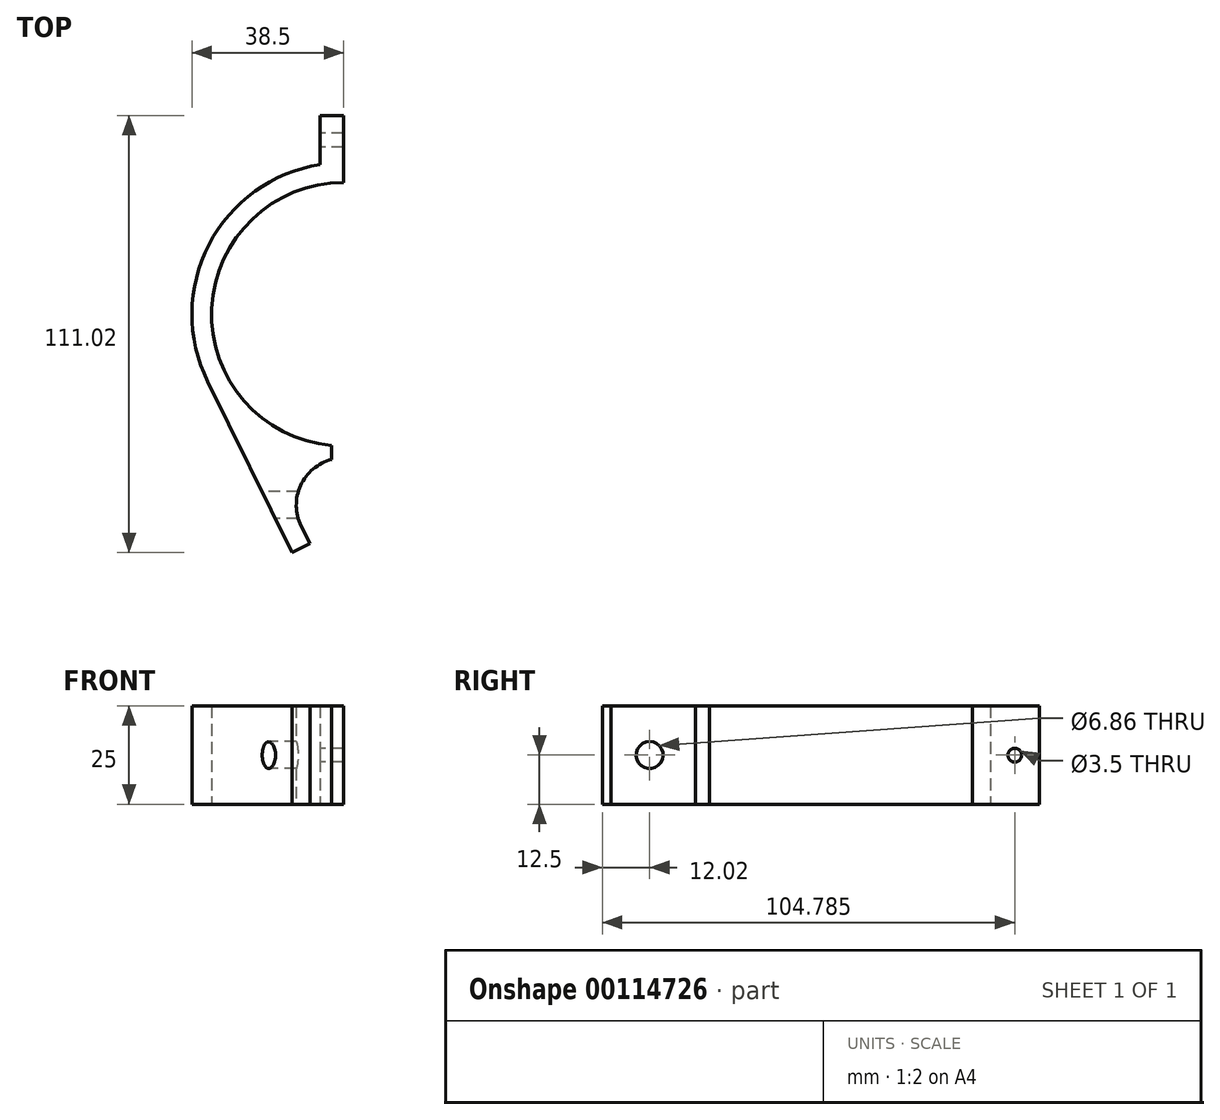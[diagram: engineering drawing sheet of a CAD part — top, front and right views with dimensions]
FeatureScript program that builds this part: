
annotation { "Feature Type Name" : "Feature", "Feature Type Description" : "" }
export const myFeature = defineFeature(function(context is Context, id is Id, definition is map)
    precondition{}
    {
        {
            var Q0;
            Q0=qCreatedBy(makeId("Top.planeOp"),FACE);
            var sketch = newSketch(context, id + "F0", { "sketchPlane" : qUnion([Q0])});
            skCircle(sketch, "E0", {"center": v(0, 0) * mm, "radius": 12 * mm});
            skCircle(sketch, "E1", {"center": v(0, 48.5) * mm, "radius": 33.5 * mm});
            skLineSegment(sketch, "E2.0", {"start": v(-34.51, 31.43) * mm, "end": v(-15.24, -7.54) * mm});
            skLineSegment(sketch, "E3.0", {"start": v(15.24, -7.54) * mm, "end": v(34.51, 31.43) * mm});
            skArc(sketch, "E4.0", {"start": v(-15.24, -7.54) * mm, "mid": v(0, -17) * mm, "end": v(15.24, -7.54) * mm});
            skArc(sketch, "E5.trimOffspring", {"start": v(34.51, 31.43) * mm, "mid": v(0, 87) * mm, "end": v(-34.51, 31.43) * mm});
            skSolve(sketch);
        }
        {
            var Q0;
            Q0 = qSketchRegion(id + "F0", true);
            extrude(context, id + "F1", {"entities" : qUnion([Q0]), "depth" : 50 * mm});
        }
        {
            var Q0;
            Q0=qCreatedBy(makeId("Front.planeOp"),FACE);
            cPlane(context, id + "F2", {"entities" : qUnion([Q0]), "cplaneType" : CPlaneType.OFFSET, "offset" : 87 * mm, "oppositeDirection" : true, "width" : 150 * mm, "height" : 150 * mm});
        }
        {
            var Q0;
            Q0=qCreatedBy(id+"F2.planeOp",FACE);
            var sketch = newSketch(context, id + "F3", { "sketchPlane" : qUnion([Q0])});
            skLineSegment(sketch, "E6.0", {"start": v(-38.5, 50) * mm, "end": v(38.5, 50) * mm});
            skEllipse(sketch, "E7", {"center": v(0, 50) * mm, "majorRadius": 23 * mm, "minorRadius": 17.5 * mm, "majorAxis": v(0, -1)});
            skSolve(sketch);
        }
        {
            var Q0;
            Q0 = qSketchRegion(id + "F3", true);
            extrude(context, id + "F4", {"entities" : qUnion([Q0]), "operationType" : NewBodyOperationType.REMOVE, "depth" : 25 * mm});
        }
        {
            var Q0;
            Q0=qCreatedBy(id+"F2.planeOp",FACE);
            var sketch = newSketch(context, id + "F5", { "sketchPlane" : qUnion([Q0])});
            skLineSegment(sketch, "E8.bottom", {"start": v(6, 0) * mm, "end": v(-6, 0) * mm});
            skLineSegment(sketch, "E8.top", {"start": v(6, 25) * mm, "end": v(-6, 25) * mm});
            skLineSegment(sketch, "E8.left", {"start": v(6, 0) * mm, "end": v(6, 25) * mm});
            skLineSegment(sketch, "E8.right", {"start": v(-6, 0) * mm, "end": v(-6, 25) * mm});
            skSolve(sketch);
        }
        {
            var Q0;
            Q0 = qSketchRegion(id + "F5", true);
            extrude(context, id + "F6", {"entities" : qUnion([Q0]), "operationType" : NewBodyOperationType.ADD, "depth" : 1 * mm});
        }
        {
            var Q0;
            Q0 = qSketchRegion(id + "F5", true);
            extrude(context, id + "F7", {"entities" : qUnion([Q0]), "operationType" : NewBodyOperationType.ADD, "oppositeDirection" : true, "depth" : 12 * mm});
        }
        {
            var Q0;
            Q0=qCreatedBy(makeId("Right.planeOp"),FACE);
            var sketch = newSketch(context, id + "F8", { "sketchPlane" : qUnion([Q0])});
            skLineSegment(sketch, "E9.0", {"start": v(31.43, 50) * mm, "end": v(-7.54, 50) * mm});
            skLineSegment(sketch, "E10.0", {"start": v(31.43, 0) * mm, "end": v(-7.54, 0) * mm});
            skPoint(sketch, "E11", {"position": v(0, 50) * mm});
            skLineSegment(sketch, "E12", {"start": v(0, 50) * mm, "end": v(0, 0) * mm, "construction": true});
            skLineSegment(sketch, "E13.0", {"start": v(86.53, 25) * mm, "end": v(99, 25) * mm, "construction": true});
            skPoint(sketch, "E14.center.orphan", {"position": v(0, 25) * mm});
            skLineSegment(sketch, "E15", {"start": v(86.53, 25) * mm, "end": v(0, 25) * mm, "construction": true});
            skLineSegment(sketch, "E16", {"start": v(0, 25) * mm, "end": v(0, 0) * mm, "construction": true});
            skCircle(sketch, "E17", {"center": v(0, 12.5) * mm, "radius": 3.43 * mm});
            skSolve(sketch);
        }
        {
            var Q0;
            Q0 = qSketchRegion(id + "F8", true);
            extrude(context, id + "F9", {"entities" : qUnion([Q0]), "operationType" : NewBodyOperationType.REMOVE, "endBound" : BoundingType.SYMMETRIC, "depth" : 60 * mm});
        }
        {
            var Q0;
            {var subQ0=sQuery(id+"F5.wireOp",EDGE,"E8.right");Q0=makeQuery(id+"F7.boolean.opBoolean","MERGE",FACE,{"derivedFrom":[makeQuery(id+"F6.opExtrude","SWEPT_FACE",FACE,{"disambiguationData":[OSD([subQ0])]}),makeQuery(id+"F7.opExtrude","SWEPT_FACE",FACE,{"disambiguationData":[OSD([subQ0])]})]});}
            var sketch = newSketch(context, id + "F10", { "sketchPlane" : qUnion([Q0])});
            skLineSegment(sketch, "E18", {"start": v(-92.76, 25) * mm, "end": v(-92.76, 0) * mm, "construction": true});
            skLineSegment(sketch, "E19", {"start": v(-99, 12.5) * mm, "end": v(-92.76, 12.5) * mm, "construction": true});
            skCircle(sketch, "E20", {"center": v(-92.76, 12.5) * mm, "radius": 1.75 * mm});
            skPoint(sketch, "E21.0.start.orphan", {"position": v(-86.53, 25) * mm});
            skPoint(sketch, "E22.orphan", {"position": v(-99, 25) * mm});
            skPoint(sketch, "E23.orphan", {"position": v(-99, 0) * mm});
            skPoint(sketch, "E24.0.start.orphan", {"position": v(-86.53, 0) * mm});
            skSolve(sketch);
        }
        {
            var Q0;
            Q0 = qSketchRegion(id + "F10", true);
            extrude(context, id + "F11", {"entities" : qUnion([Q0]), "operationType" : NewBodyOperationType.REMOVE, "oppositeDirection" : true, "depth" : 25 * mm});
        }
        {
            var Q0;
            Q0=makeQuery(id+"F1.opExtrude","CAP_FACE",FACE,{"disambiguationData":[OSD([sQuery(id+"F0.wireOp",EDGE,"E0"),sQuery(id+"F0.wireOp",EDGE,"E1"),sQuery(id+"F0.wireOp",EDGE,"E2.0"),sQuery(id+"F0.wireOp",EDGE,"E3.0"),sQuery(id+"F0.wireOp",EDGE,"E4.0"),sQuery(id+"F0.wireOp",EDGE,"E5.trimOffspring")])],"isStart":false});
            var sketch = newSketch(context, id + "F12", { "sketchPlane" : qUnion([Q0])});
            skLineSegment(sketch, "E25.bottom", {"start": v(-3, 17.8) * mm, "end": v(3, 17.8) * mm});
            skLineSegment(sketch, "E25.top", {"start": v(-3, 9.03) * mm, "end": v(3, 9.03) * mm});
            skLineSegment(sketch, "E25.left", {"start": v(-3, 17.8) * mm, "end": v(-3, 9.03) * mm});
            skLineSegment(sketch, "E25.right", {"start": v(3, 17.8) * mm, "end": v(3, 9.03) * mm});
            skSolve(sketch);
        }
        {
            var Q0;
            Q0 = qSketchRegion(id + "F12", true);
            extrude(context, id + "F13", {"entities" : qUnion([Q0]), "operationType" : NewBodyOperationType.REMOVE, "oppositeDirection" : true, "depth" : 55 * mm});
        }
        {
            var Q0;
            Q0=makeQuery(id+"F1.opExtrude","CAP_FACE",FACE,{"disambiguationData":[OSD([sQuery(id+"F0.wireOp",EDGE,"E0"),sQuery(id+"F0.wireOp",EDGE,"E1"),sQuery(id+"F0.wireOp",EDGE,"E2.0"),sQuery(id+"F0.wireOp",EDGE,"E3.0"),sQuery(id+"F0.wireOp",EDGE,"E4.0"),sQuery(id+"F0.wireOp",EDGE,"E5.trimOffspring")])],"isStart":false});
            var sketch = newSketch(context, id + "F14", { "sketchPlane" : qUnion([Q0])});
            skArc(sketch, "E26.0", {"start": v(-10.76, -5.32) * mm, "mid": v(0, -12) * mm, "end": v(10.76, -5.32) * mm});
            skArc(sketch, "E27.0", {"start": v(-15.24, -7.54) * mm, "mid": v(0, -17) * mm, "end": v(15.24, -7.54) * mm});
            skLineSegment(sketch, "E28", {"start": v(-15.24, -7.54) * mm, "end": v(-10.76, -5.32) * mm});
            skLineSegment(sketch, "E29", {"start": v(15.24, -7.54) * mm, "end": v(10.76, -5.32) * mm});
            skPoint(sketch, "E30.orphan", {"position": v(3, 11.62) * mm});
            skPoint(sketch, "E31.orphan", {"position": v(-3, 11.62) * mm});
            skSolve(sketch);
        }
        {
            var Q0;
            Q0 = qSketchRegion(id + "F14", true);
            extrude(context, id + "F15", {"entities" : qUnion([Q0]), "operationType" : NewBodyOperationType.REMOVE, "oppositeDirection" : true, "depth" : 52 * mm});
        }
        {
            var Q0;
            Q0=qCreatedBy(makeId("Top.planeOp"),FACE);
            var sketch = newSketch(context, id + "F16", { "sketchPlane" : qUnion([Q0])});
            skLineSegment(sketch, "E32.0", {"start": v(-15.24, -7.54) * mm, "end": v(-10.76, -5.32) * mm});
            skLineSegment(sketch, "E33", {"start": v(-15.24, -7.54) * mm, "end": v(-13.02, -12.02) * mm});
            skLineSegment(sketch, "E34", {"start": v(-10.76, -5.32) * mm, "end": v(-8.54, -9.8) * mm});
            skLineSegment(sketch, "E35", {"start": v(-13.02, -12.02) * mm, "end": v(-8.54, -9.8) * mm});
            skPoint(sketch, "E36.0.end.orphan", {"position": v(10.76, -5.32) * mm});
            skPoint(sketch, "E37.0.end.orphan", {"position": v(34.51, 31.43) * mm});
            skPoint(sketch, "E37.0.start.orphan", {"position": v(15.24, -7.54) * mm});
            skPoint(sketch, "E38.0.start.orphan", {"position": v(-34.51, 31.43) * mm});
            skLineSegment(sketch, "E39.MirrorCS", {"start": v(15.24, -7.54) * mm, "end": v(10.76, -5.32) * mm});
            skLineSegment(sketch, "E40.MirrorCS", {"start": v(10.76, -5.32) * mm, "end": v(8.54, -9.8) * mm});
            skLineSegment(sketch, "E41.MirrorCS", {"start": v(13.02, -12.02) * mm, "end": v(8.54, -9.8) * mm});
            skLineSegment(sketch, "E42.MirrorCS", {"start": v(15.24, -7.54) * mm, "end": v(13.02, -12.02) * mm});
            skSolve(sketch);
        }
        {
            var Q0;
            Q0 = qSketchRegion(id + "F16", true);
            extrude(context, id + "F17", {"entities" : qUnion([Q0]), "operationType" : NewBodyOperationType.ADD, "depth" : 50 * mm});
        }
        {
            var Q0;
            Q0=qCreatedBy(makeId("Top.planeOp"),FACE);
            var sketch = newSketch(context, id + "F18", { "sketchPlane" : qUnion([Q0])});
            skLineSegment(sketch, "E43.bottom", {"start": v(0, -47.13) * mm, "end": v(81.3, -47.13) * mm});
            skLineSegment(sketch, "E43.top", {"start": v(0, 114.66) * mm, "end": v(81.3, 114.66) * mm});
            skLineSegment(sketch, "E43.left", {"start": v(0, -47.13) * mm, "end": v(0, 114.66) * mm});
            skLineSegment(sketch, "E43.right", {"start": v(81.3, -47.13) * mm, "end": v(81.3, 114.66) * mm});
            skSolve(sketch);
        }
        {
            var Q0;
            Q0 = qSketchRegion(id + "F18", true);
            extrude(context, id + "F19", {"entities" : qUnion([Q0]), "operationType" : NewBodyOperationType.REMOVE, "depth" : 50 * mm});
        }
        {
            var Q0;
            Q0=qCreatedBy(makeId("Front.planeOp"),FACE);
            var sketch = newSketch(context, id + "F20", { "sketchPlane" : qUnion([Q0])});
            skPoint(sketch, "E44.0", {"position": v(0, 25) * mm});
            skLineSegment(sketch, "E45.bottom", {"start": v(0, 25) * mm, "end": v(-42.07, 25) * mm});
            skLineSegment(sketch, "E45.top", {"start": v(0, 54.02) * mm, "end": v(-42.07, 54.02) * mm});
            skLineSegment(sketch, "E45.left", {"start": v(0, 25) * mm, "end": v(0, 54.02) * mm});
            skLineSegment(sketch, "E45.right", {"start": v(-42.07, 25) * mm, "end": v(-42.07, 54.02) * mm});
            skSolve(sketch);
        }
        {
            var Q0;
            Q0 = qSketchRegion(id + "F20", true);
            extrude(context, id + "F21", {"entities" : qUnion([Q0]), "operationType" : NewBodyOperationType.REMOVE, "endBound" : BoundingType.SYMMETRIC, "oppositeDirection" : true, "depth" : 500 * mm});
        }
    });
